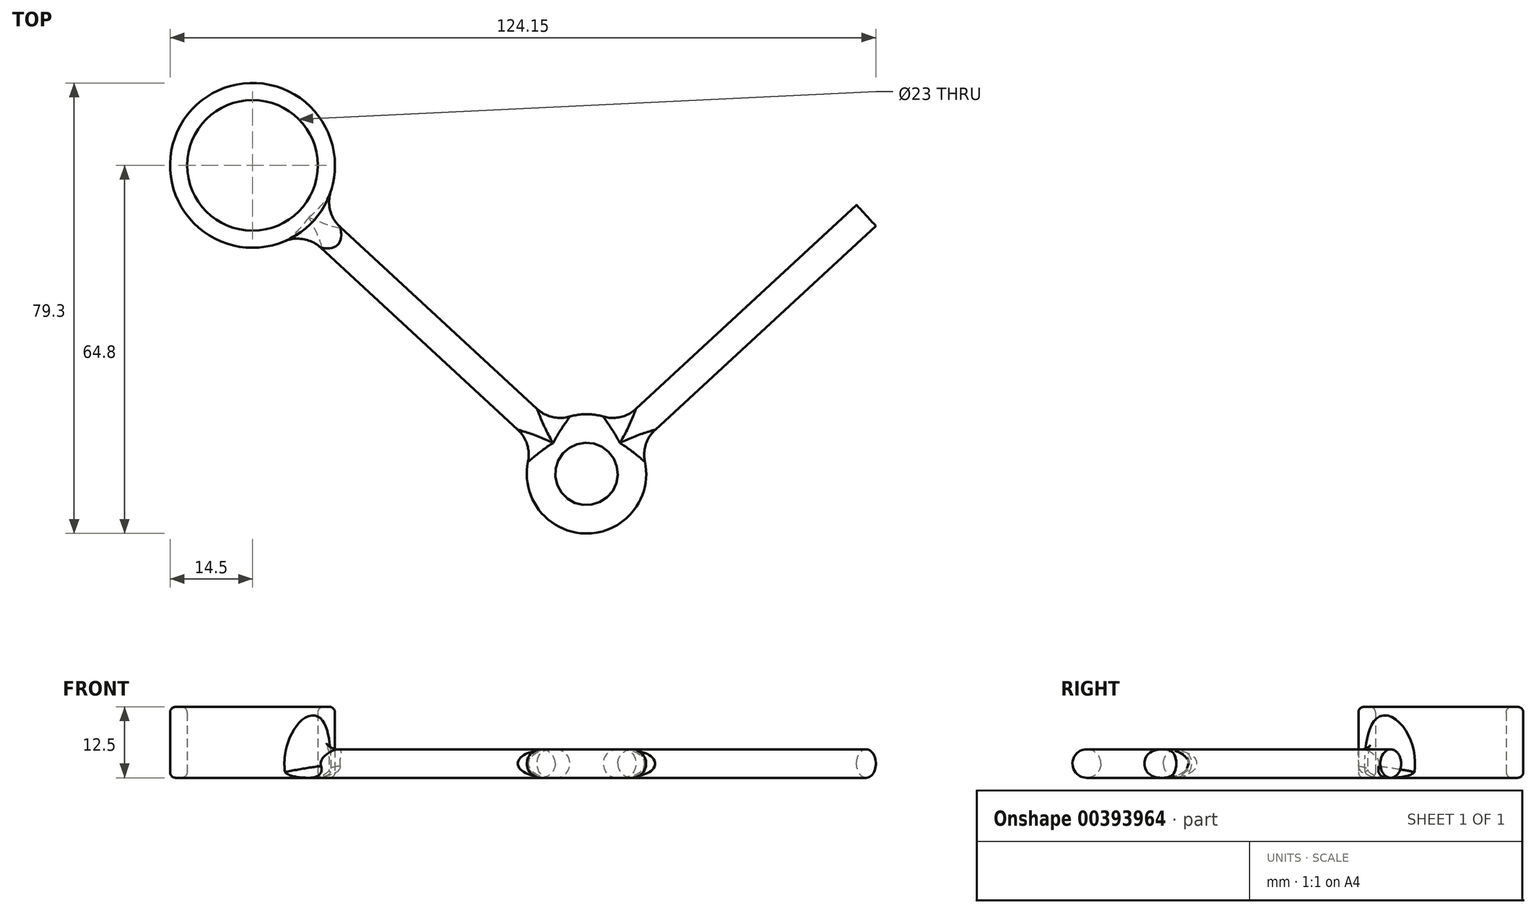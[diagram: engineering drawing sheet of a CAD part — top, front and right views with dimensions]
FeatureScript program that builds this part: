
annotation { "Feature Type Name" : "Feature", "Feature Type Description" : "" }
export const myFeature = defineFeature(function(context is Context, id is Id, definition is map)
    precondition{}
    {
        {
            var Q0;
            Q0=qCreatedBy(makeId("Top.planeOp"),FACE);
            var sketch = newSketch(context, id + "F0", { "sketchPlane" : qUnion([Q0])});
            skCircle(sketch, "E0", {"center": v(-58.75, 54.3) * mm, "radius": 11.5 * mm});
            skCircle(sketch, "E1", {"center": v(-58.75, 54.3) * mm, "radius": 14.5 * mm});
            skPoint(sketch, "E2", {"position": v(-47.25, 54.3) * mm});
            skPoint(sketch, "E3", {"position": v(-44.25, 54.3) * mm});
            skCircle(sketch, "E4.MirrorC", {"center": v(58.75, 54.3) * mm, "radius": 14.5 * mm});
            skCircle(sketch, "E5.MirrorC", {"center": v(58.75, 54.3) * mm, "radius": 11.5 * mm});
            skCircle(sketch, "E6", {"center": v(0, 0) * mm, "radius": 8 * mm});
            skLineSegment(sketch, "E7", {"start": v(-58.75, 54.3) * mm, "end": v(-50.3, 46.5) * mm, "construction": true});
            skLineSegment(sketch, "E8", {"start": v(-50.3, 46.5) * mm, "end": v(-48.1, 44.46) * mm, "construction": true});
            skLineSegment(sketch, "E9", {"start": v(-48.1, 44.46) * mm, "end": v(-5.87, 5.43) * mm, "construction": true});
            skPoint(sketch, "E10", {"position": v(-49.2, 45.48) * mm});
            skLineSegment(sketch, "E11", {"start": v(-5.87, 5.43) * mm, "end": v(-49.2, 45.48) * mm});
            skLineSegment(sketch, "E12.MirrorCS", {"start": v(5.87, 5.43) * mm, "end": v(49.2, 45.48) * mm});
            skSolve(sketch);
        }
        {
            var Q0;
            Q0=makeQuery(id+"F0.imprint","IMPRINT",FACE,{"disambiguationData":[TD([[makeQuery(id+"F0.imprint","IMPRINT",EDGE,{"derivedFrom":sQuery(id+"F0.wireOp",EDGE,"E0")}),-1.0]])]});
            var Q1;
            Q1=makeQuery(id+"F0.imprint","IMPRINT",FACE,{"disambiguationData":[TD([[makeQuery(id+"F0.imprint","IMPRINT",EDGE,{"derivedFrom":sQuery(id+"F0.wireOp",EDGE,"E4.MirrorC")}),-1.0]])]});
            extrude(context, id + "F1", {"entities" : qUnion([Q0, Q1]), "depth" : 10 * mm, "hasSecondDirection" : true, "secondDirectionOppositeDirection" : true, "secondDirectionDepth" : 2.5 * mm});
        }
        {
            var Q0;
            Q0=makeQuery(id+"F1.opExtrude","CAP_FACE",FACE,{"disambiguationData":[OSD([sQuery(id+"F0.wireOp",EDGE,"E0"),sQuery(id+"F0.wireOp",EDGE,"E1")])],"isStart":false});
            var Q1;
            Q1=makeQuery(id+"F1.opExtrude","CAP_FACE",FACE,{"disambiguationData":[OSD([sQuery(id+"F0.wireOp",EDGE,"E0"),sQuery(id+"F0.wireOp",EDGE,"E1")])],"isStart":true});
            var Q2;
            Q2=makeQuery(id+"F1.opExtrude","CAP_FACE",FACE,{"disambiguationData":[OSD([sQuery(id+"F0.wireOp",EDGE,"E4.MirrorC"),sQuery(id+"F0.wireOp",EDGE,"E5.MirrorC")])],"isStart":true});
            var Q3;
            Q3=makeQuery(id+"F1.opExtrude","CAP_FACE",FACE,{"disambiguationData":[OSD([sQuery(id+"F0.wireOp",EDGE,"E4.MirrorC"),sQuery(id+"F0.wireOp",EDGE,"E5.MirrorC")])],"isStart":false});
            fillet(context, id + "F2", {"entities" : qUnion([Q0, Q1, Q2, Q3]), "radius" : 1 * mm, "tangentPropagation" : true, "allowEdgeOverflow" : false});
        }
        {
            var Q0;
            Q0=qCreatedBy(makeId("Front.planeOp"),FACE);
            var sketch = newSketch(context, id + "F3", { "sketchPlane" : qUnion([Q0])});
            skLineSegment(sketch, "E13.0", {"start": v(-8, 0) * mm, "end": v(8, 0) * mm, "construction": true});
            skCircle(sketch, "E14", {"center": v(-8, 0) * mm, "radius": 2.5 * mm});
            skSolve(sketch);
        }
        {
            var Q0;
            Q0=makeQuery(id+"F3.imprint","IMPRINT",FACE,{"disambiguationData":[TD([[makeQuery(id+"F3.imprint","IMPRINT",EDGE,{"derivedFrom":sQuery(id+"F3.wireOp",EDGE,"E14")}),1.0]])]});
            var Q1;
            Q1=sQuery(id+"F0.wireOp",EDGE,"E6");
            sweep(context, id + "F4", {"profiles" : qUnion([Q0]), "path" : qUnion([Q1])});
        }
        {
            var Q0;
            Q0=sQuery(id+"F0.wireOp",EDGE,"E11");
            var Q1;
            Q1=sQuery(id+"F0.wireOp",VERTEX,"E10");
            cPlane(context, id + "F5", {"entities" : qUnion([Q0, Q1]), "cplaneType" : CPlaneType.CURVE_POINT, "offset" : 25 * mm, "width" : 150 * mm, "height" : 150 * mm});
        }
        {
            var Q0;
            Q0=qCreatedBy(id+"F5.planeOp",FACE);
            var sketch = newSketch(context, id + "F6", { "sketchPlane" : qUnion([Q0])});
            skCircle(sketch, "E15", {"center": v(0, 0) * mm, "radius": 2.5 * mm});
            skSolve(sketch);
        }
        {
            var Q0;
            Q0 = qSketchRegion(id + "F6", true);
            var Q1;
            Q1=sQuery(id+"F0.wireOp",EDGE,"E11");
            sweep(context, id + "F7", {"operationType" : NewBodyOperationType.ADD, "profiles" : qUnion([Q0]), "path" : qUnion([Q1])});
        }
        {
            var Q0;
            Q0=sQuery(id+"F0.wireOp",EDGE,"E12.MirrorCS");
            var Q1;
            Q1=sQuery(id+"F0.wireOp",VERTEX,"E12.MirrorCS.end");
            cPlane(context, id + "F8", {"entities" : qUnion([Q0, Q1]), "cplaneType" : CPlaneType.CURVE_POINT, "offset" : 25 * mm, "width" : 150 * mm, "height" : 150 * mm});
        }
        {
            var Q0;
            Q0=qCreatedBy(id+"F8.planeOp",FACE);
            var sketch = newSketch(context, id + "F9", { "sketchPlane" : qUnion([Q0])});
            skCircle(sketch, "E16", {"center": v(0, 0) * mm, "radius": 2.5 * mm});
            skSolve(sketch);
        }
        {
            var Q0;
            Q0 = qSketchRegion(id + "F9", true);
            var Q1;
            Q1=sQuery(id+"F0.wireOp",EDGE,"E12.MirrorCS");
            sweep(context, id + "F10", {"operationType" : NewBodyOperationType.ADD, "profiles" : qUnion([Q0]), "path" : qUnion([Q1])});
        }
        {
            var Q0;
            Q0=makeQuery(id+"F7.boolean.opBoolean","INTERSECT",EDGE,{"derivedFrom":[makeQuery(id+"F1.opExtrude","SWEPT_FACE",FACE,{"disambiguationData":[OSD([sQuery(id+"F0.wireOp",EDGE,"E1")])]}),makeQuery(id+"F7.opSweep","SWEPT_FACE",FACE,{"disambiguationData":[OSD([sQuery(id+"F0.wireOp",EDGE,"E11"),sQuery(id+"F6.wireOp",EDGE,"E15")])]})]});
            var Q1;
            Q1=makeQuery(id+"F10.boolean.opBoolean","INTERSECT",EDGE,{"derivedFrom":[makeQuery(id+"F1.opExtrude","SWEPT_FACE",FACE,{"disambiguationData":[OSD([sQuery(id+"F0.wireOp",EDGE,"E4.MirrorC")])]}),makeQuery(id+"F10.opSweep","SWEPT_FACE",FACE,{"disambiguationData":[OSD([sQuery(id+"F0.wireOp",EDGE,"E12.MirrorCS"),sQuery(id+"F9.wireOp",EDGE,"E16")])]})]});
            var Q2;
            Q2=makeQuery(id+"F10.boolean.opBoolean","INTERSECT",EDGE,{"disambiguationData":[OD(0.0)],"derivedFrom":[makeQuery(id+"F4.opSweep","SWEPT_FACE",FACE,{"disambiguationData":[OSD([sQuery(id+"F0.wireOp",EDGE,"E6"),sQuery(id+"F3.wireOp",EDGE,"E14")])]}),makeQuery(id+"F10.opSweep","SWEPT_FACE",FACE,{"disambiguationData":[OSD([sQuery(id+"F0.wireOp",EDGE,"E12.MirrorCS"),sQuery(id+"F9.wireOp",EDGE,"E16")])]})]});
            var Q3;
            Q3=makeQuery(id+"F10.boolean.opBoolean","INTERSECT",EDGE,{"disambiguationData":[OD(1.0)],"derivedFrom":[makeQuery(id+"F4.opSweep","SWEPT_FACE",FACE,{"disambiguationData":[OSD([sQuery(id+"F0.wireOp",EDGE,"E6"),sQuery(id+"F3.wireOp",EDGE,"E14")])]}),makeQuery(id+"F10.opSweep","SWEPT_FACE",FACE,{"disambiguationData":[OSD([sQuery(id+"F0.wireOp",EDGE,"E12.MirrorCS"),sQuery(id+"F9.wireOp",EDGE,"E16")])]})]});
            var Q4;
            Q4=makeQuery(id+"F7.boolean.opBoolean","INTERSECT",EDGE,{"disambiguationData":[OD(1.0)],"derivedFrom":[makeQuery(id+"F4.opSweep","SWEPT_FACE",FACE,{"disambiguationData":[OSD([sQuery(id+"F0.wireOp",EDGE,"E6"),sQuery(id+"F3.wireOp",EDGE,"E14")])]}),makeQuery(id+"F7.opSweep","SWEPT_FACE",FACE,{"disambiguationData":[OSD([sQuery(id+"F0.wireOp",EDGE,"E11"),sQuery(id+"F6.wireOp",EDGE,"E15")])]})]});
            var Q5;
            Q5=makeQuery(id+"F7.boolean.opBoolean","INTERSECT",EDGE,{"disambiguationData":[OD(0.0)],"derivedFrom":[makeQuery(id+"F4.opSweep","SWEPT_FACE",FACE,{"disambiguationData":[OSD([sQuery(id+"F0.wireOp",EDGE,"E6"),sQuery(id+"F3.wireOp",EDGE,"E14")])]}),makeQuery(id+"F7.opSweep","SWEPT_FACE",FACE,{"disambiguationData":[OSD([sQuery(id+"F0.wireOp",EDGE,"E11"),sQuery(id+"F6.wireOp",EDGE,"E15")])]})]});
            fillet(context, id + "F11", {"entities" : qUnion([Q0, Q1, Q2, Q3, Q4, Q5]), "radius" : 6 * mm, "tangentPropagation" : true, "allowEdgeOverflow" : false});
        }
    });
